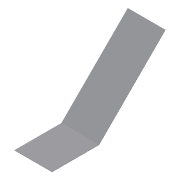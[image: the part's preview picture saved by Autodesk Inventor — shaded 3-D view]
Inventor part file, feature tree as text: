
AUTODESK INVENTOR PART (.ipt)
format: ipt  version: 2016 (Build 200138000, 138)  size: 86,016 bytes
history: native  units: mm
features: sheet_metal_op x4, sketch x2, other x2
ambient origin geometry x8: Origin, YZ Plane, XZ Plane, XY Plane, X Axis, Y Axis, Z Axis, Center Point
bodies: Solid1 (feature_tree)
feature tree (8):
  sheet_metal_op  "Face1"
  sheet_metal_op  "Flange1"
  sketch  "Sketch1"  dims[d0=80.0mm]
  other  "Plate1"
  sketch  "Sketch2"  dims[d1=100.0mm d2=0.5mm d3=0.5mm d4=0.25mm d5=1.0mm d6=0.5mm d7=200.0mm d8=45.0deg d9=0.5mm d10=2.0mm d11=0.5mm d12=0.5mm]
  other  "Plate2"
  sheet_metal_op  "Bend1"
  sheet_metal_op  "Corner1"
